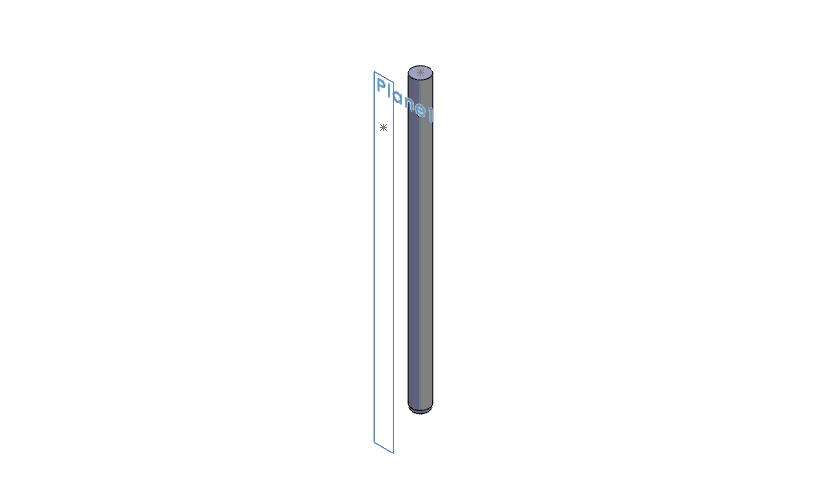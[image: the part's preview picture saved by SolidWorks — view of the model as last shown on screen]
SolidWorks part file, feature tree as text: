
SOLIDWORKS PART (.sldprt)
format: sldprt  version: not decoded by parser v0  size: 130,560 bytes
history: native  units: mm
features: sketch x5, material x1, extrude x1, plane x1, hole x1, fillet x1 (+12 scaffold rows collapsed)
feature tree (22):
  scaffold x12  (default folders/planes/origin — collapsed)
  material  "Material <not specified>"
  sketch  "Sketch1"  dims[D1=3.0mm]
  extrude  "Boss-Extrude1"  Depth=100mm
  sketch  "Sketch2"
  plane  "Plane1"  Offset=12.54mm
  sketch  "Sketch3"  dims[D1=10.0mm]
  hole  "Ø1.5mm Dowel Hole5"  Diameter=1.5mm Depth=20mm
  sketch  "3DSketch4"  dims[D1=~10.611629mm]
  sketch  "Sketch7"  dims[hole-wizard template sketch: 47 standard entries collapsed; hole parameters kept: c15.Hole Depth=20.0mm c15.D3=~14.816244mm c15.Drill Angle=118.0deg]
  fillet  "Fillet1"  Radius=2mm
decode coverage: 7 of 8 modeling features carry decoded parameters
note: ~ marks probable driven/reference dimensions
note: suppression state not decoded; provenance and decode notes live in map.json
